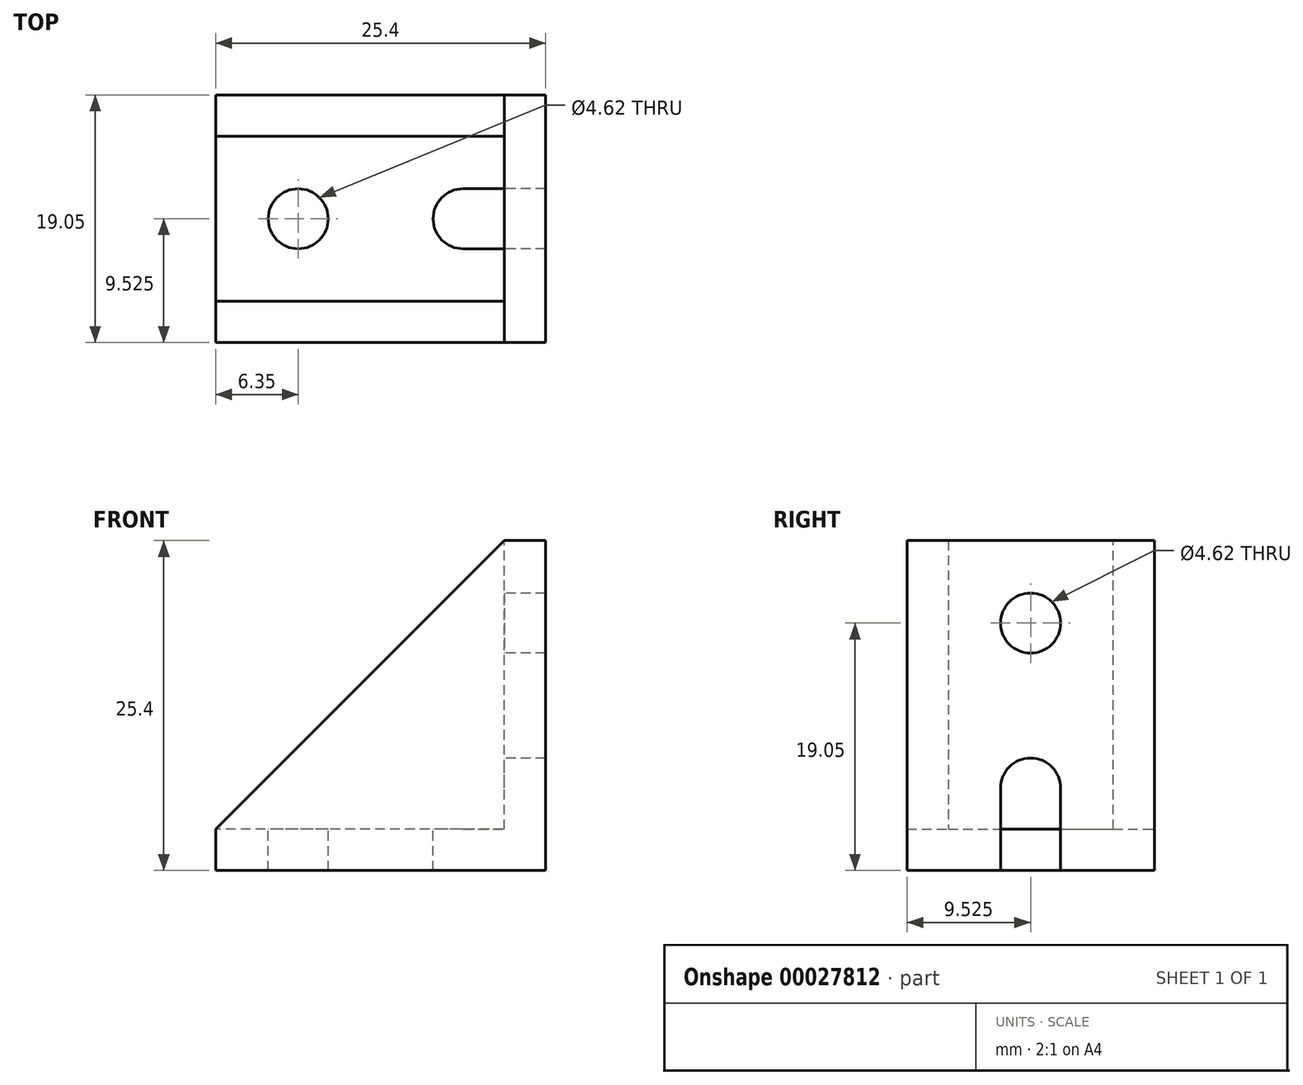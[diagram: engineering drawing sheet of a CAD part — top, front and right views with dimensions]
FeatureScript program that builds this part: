
annotation { "Feature Type Name" : "Feature", "Feature Type Description" : "" }
export const myFeature = defineFeature(function(context is Context, id is Id, definition is map)
    precondition{}
    {
        {
            var Q0;
            Q0=qCreatedBy(makeId("Front.planeOp"),FACE);
            var sketch = newSketch(context, id + "F0", { "sketchPlane" : qUnion([Q0])});
            skLineSegment(sketch, "E0", {"start": v(0, 0) * mm, "end": v(25.4, 0) * mm});
            skLineSegment(sketch, "E1", {"start": v(25.4, 0) * mm, "end": v(25.4, 25.4) * mm});
            skLineSegment(sketch, "E2", {"start": v(25.4, 25.4) * mm, "end": v(22.23, 25.4) * mm});
            skLineSegment(sketch, "E3", {"start": v(0, 0) * mm, "end": v(0, 3.18) * mm});
            skLineSegment(sketch, "E4", {"start": v(0, 3.18) * mm, "end": v(22.23, 25.4) * mm});
            skSolve(sketch);
        }
        {
            var Q0;
            Q0 = qSketchRegion(id + "F0", true);
            extrude(context, id + "F1", {"entities" : qUnion([Q0]), "depth" : 19.05 * mm});
        }
        {
            var Q0;
            Q0=makeQuery(id+"F1.opExtrude","SWEPT_FACE",FACE,{"disambiguationData":[OSD([sQuery(id+"F0.wireOp",EDGE,"E3")])]});
            var sketch = newSketch(context, id + "F2", { "sketchPlane" : qUnion([Q0])});
            skLineSegment(sketch, "E5", {"start": v(3.17, 3.17) * mm, "end": v(3.17, 25.4) * mm});
            skLineSegment(sketch, "E6", {"start": v(3.17, 25.4) * mm, "end": v(15.88, 25.4) * mm});
            skLineSegment(sketch, "E7", {"start": v(15.88, 25.4) * mm, "end": v(15.88, 3.17) * mm});
            skLineSegment(sketch, "E8", {"start": v(15.88, 3.17) * mm, "end": v(3.17, 3.17) * mm});
            skSolve(sketch);
        }
        {
            var Q0;
            Q0 = qSketchRegion(id + "F2", true);
            extrude(context, id + "F3", {"entities" : qUnion([Q0]), "operationType" : NewBodyOperationType.REMOVE, "oppositeDirection" : true, "depth" : 22.22 * mm});
        }
        {
            var Q0;
            Q0=makeQuery(id+"F3.boolean.opBoolean","COPY",FACE,{"derivedFrom":makeQuery(id+"F3.opExtrude","SWEPT_FACE",FACE,{"disambiguationData":[OSD([sQuery(id+"F2.wireOp",EDGE,"E8")])]})});
            var sketch = newSketch(context, id + "F4", { "sketchPlane" : qUnion([Q0])});
            skPoint(sketch, "E9", {"position": v(22.23, -9.53) * mm});
            skPoint(sketch, "E10", {"position": v(21.36, -9.53) * mm});
            skCircle(sketch, "E11", {"center": v(19.05, -9.53) * mm, "radius": 2.31 * mm});
            skCircle(sketch, "E12", {"center": v(6.35, -9.53) * mm, "radius": 2.31 * mm});
            skLineSegment(sketch, "E13", {"start": v(19.05, -9.53) * mm, "end": v(19.05, -11.84) * mm});
            skLineSegment(sketch, "E14", {"start": v(19.05, -9.53) * mm, "end": v(19.05, -7.21) * mm});
            skLineSegment(sketch, "E15", {"start": v(19.05, -7.21) * mm, "end": v(22.23, -7.21) * mm});
            skLineSegment(sketch, "E16", {"start": v(19.05, -11.84) * mm, "end": v(22.23, -11.84) * mm});
            skSolve(sketch);
        }
        {
            var Q0;
            Q0 = qSketchRegion(id + "F4", true);
            var Q1;
            {var subQ2=sQuery(id+"F4.wireOp",EDGE,"E15");Q1=makeQuery(id+"F4.imprint","IMPRINT",FACE,{"disambiguationData":[TD([[makeQuery(id+"F4.imprint","IMPRINT",EDGE,{"derivedFrom":subQ2}),-1.0]])]});}
            extrude(context, id + "F5", {"entities" : qUnion([Q0, Q1]), "operationType" : NewBodyOperationType.REMOVE, "oppositeDirection" : true, "depth" : 3.17 * mm});
        }
        {
            var Q0;
            {var subQ0=sQuery(id+"F2.wireOp",EDGE,"E8");Q0=makeQuery(id+"F5.boolean.opBoolean","MERGE",FACE,{"derivedFrom":[makeQuery(id+"F3.boolean.opBoolean","COPY",FACE,{"derivedFrom":makeQuery(id+"F3.opExtrude","CAP_FACE",FACE,{"disambiguationData":[OSD([sQuery(id+"F2.wireOp",EDGE,"E5"),sQuery(id+"F2.wireOp",EDGE,"E6"),sQuery(id+"F2.wireOp",EDGE,"E7"),subQ0])],"isStart":false})}),makeQuery(id+"F5.opExtrude","SWEPT_FACE",FACE,{"disambiguationData":[OSD([subQ0])]})]});}
            var sketch = newSketch(context, id + "F6", { "sketchPlane" : qUnion([Q0])});
            skPoint(sketch, "E17", {"position": v(9.53, 3.17) * mm});
            skPoint(sketch, "E18", {"position": v(9.53, 4.04) * mm});
            skCircle(sketch, "E19", {"center": v(9.53, 6.35) * mm, "radius": 2.31 * mm});
            skCircle(sketch, "E20", {"center": v(9.52, 19.05) * mm, "radius": 2.31 * mm});
            skLineSegment(sketch, "E21", {"start": v(9.53, 6.35) * mm, "end": v(11.84, 6.35) * mm});
            skLineSegment(sketch, "E22", {"start": v(9.53, 6.35) * mm, "end": v(7.21, 6.35) * mm});
            skLineSegment(sketch, "E23", {"start": v(7.21, 6.35) * mm, "end": v(7.21, 3.17) * mm});
            skLineSegment(sketch, "E24", {"start": v(11.84, 6.35) * mm, "end": v(11.84, 3.17) * mm});
            skSolve(sketch);
        }
        {
            var Q0;
            Q0 = qSketchRegion(id + "F6", true);
            var Q1;
            {var subQ2=sQuery(id+"F6.wireOp",EDGE,"E23");Q1=makeQuery(id+"F6.imprint","IMPRINT",FACE,{"disambiguationData":[TD([[makeQuery(id+"F6.imprint","IMPRINT",EDGE,{"derivedFrom":subQ2}),1.0]])]});}
            extrude(context, id + "F7", {"entities" : qUnion([Q0, Q1]), "operationType" : NewBodyOperationType.REMOVE, "oppositeDirection" : true, "depth" : 3.17 * mm});
        }
    });
